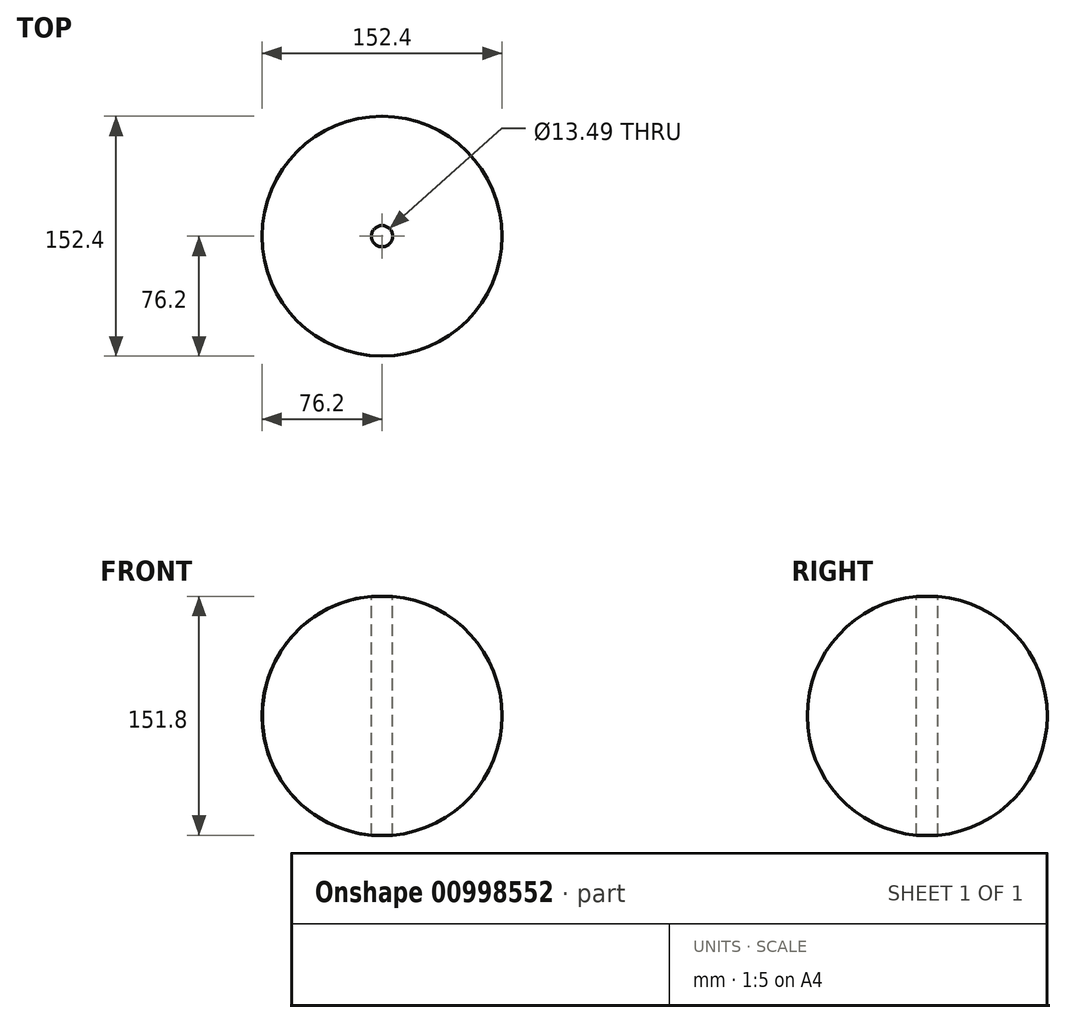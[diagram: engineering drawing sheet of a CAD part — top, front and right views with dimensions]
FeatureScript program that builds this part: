
annotation { "Feature Type Name" : "Feature", "Feature Type Description" : "" }
export const myFeature = defineFeature(function(context is Context, id is Id, definition is map)
    precondition{}
    {
        {
            var Q0;
            Q0=qCreatedBy(makeId("Front.planeOp"),FACE);
            var sketch = newSketch(context, id + "F0", { "sketchPlane" : qUnion([Q0])});
            skArc(sketch, "E0", {"start": v(-6.35, 75.93) * mm, "mid": v(-76.2, 0) * mm, "end": v(-6.35, -75.93) * mm});
            skLineSegment(sketch, "E1", {"start": v(0, 75.93) * mm, "end": v(0, -75.93) * mm});
            skLineSegment(sketch, "E2", {"start": v(0, 0) * mm, "end": v(-6.35, 0) * mm});
            skLineSegment(sketch, "E3", {"start": v(-6.35, 0) * mm, "end": v(-6.35, 75.93) * mm});
            skLineSegment(sketch, "E4", {"start": v(-6.35, 75.93) * mm, "end": v(0, 75.93) * mm});
            skLineSegment(sketch, "E5", {"start": v(0, -75.93) * mm, "end": v(-6.35, -75.93) * mm});
            skLineSegment(sketch, "E6", {"start": v(-6.35, -75.93) * mm, "end": v(-6.35, 0) * mm});
            skPoint(sketch, "E7.orphan", {"position": v(0, 76.2) * mm});
            skSolve(sketch);
        }
        {
            var Q0;
            {var subQ0=sQuery(id+"F0.wireOp",EDGE,"E1");Q0=makeQuery(id+"F0.imprint","IMPRINT",FACE,{"disambiguationData":[TD([[makeQuery(id+"F0.imprint","IMPRINT",EDGE,{"derivedFrom":subQ0}),-1.0]])]});}
            var Q1;
            Q1=makeQuery(id+"F0.imprint","IMPRINT",FACE,{"disambiguationData":[TD([[makeQuery(id+"F0.imprint","IMPRINT",EDGE,{"derivedFrom":sQuery(id+"F0.wireOp",EDGE,"E0")}),1.0]])]});
            var Q2;
            Q2=sQuery(id+"F0.wireOp",EDGE,"E1");
            revolve(context, id + "F1", {"surfaceOperationType" : NewSurfaceOperationType.NEW, "entities" : qUnion([Q0, Q1]), "axis" : qUnion([Q2]), "revolveType" : RevolveType.FULL});
        }
        {
            var Q0;
            Q0=makeQuery(id+"F1.opRevolve","SWEPT_FACE",FACE,{"disambiguationData":[OSD([sQuery(id+"F0.wireOp",EDGE,"E4")])]});
            var sketch = newSketch(context, id + "F2", { "sketchPlane" : qUnion([Q0])});
            skLineSegment(sketch, "E8", {"start": v(0, 0) * mm, "end": v(-1.43, 1.93) * mm});
            skSolve(sketch);
        }
        {
            var Q0;
            Q0=sQuery(id+"F2.wireOp",VERTEX,"E8.start");
            var Q1;
            Q1=makeQuery(id+"F1.opRevolve","SWEPT_BODY",BODY,{"disambiguationData":[OSD([sQuery(id+"F0.wireOp",EDGE,"E0"),sQuery(id+"F0.wireOp",EDGE,"E1"),sQuery(id+"F0.wireOp",EDGE,"E4"),sQuery(id+"F0.wireOp",EDGE,"E5")])]});
            hole(context, id + "F3", {"style" : HoleStyle.SIMPLE, "endStyle" : HoleEndStyle.THROUGH, "standardTappedOrClearance" : lookupTablePath({ "fit" : "Close (ASME)", "standard" : "ANSI", "size" : "1/2", "type" : "Clearance" }), "standardBlindInLast" : lookupTablePath({ "fit" : "Close", "standard" : "ANSI", "engagement" : "75%", "pitch" : "13 tpi", "size" : "1/2", "type" : "Clearance & tapped" }), "holeDiameter" : 13.5 * mm, "majorDiameter" : 12.7 * mm, "isTappedThrough" : true, "tappedDepth" : 21.59 * mm, "tapClearance" : 3, "startFromSketch" : true, "locations" : qUnion([Q0]), "scope" : qUnion([Q1])});
        }
    });
